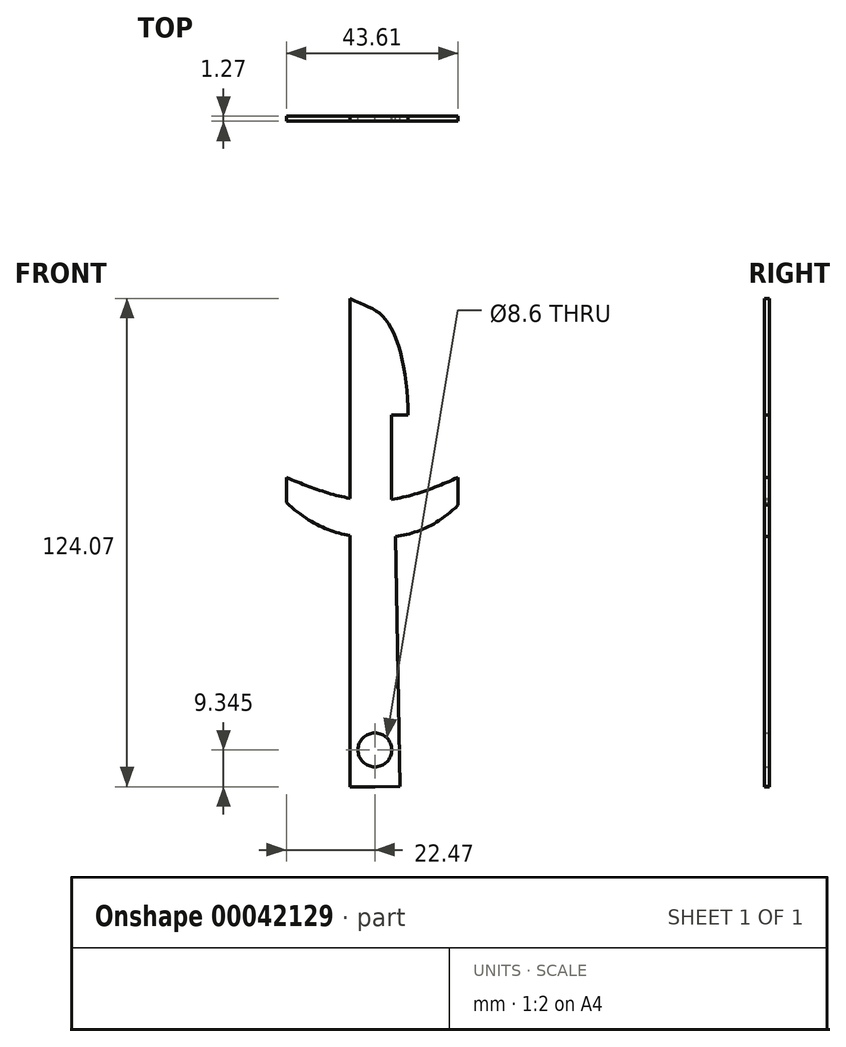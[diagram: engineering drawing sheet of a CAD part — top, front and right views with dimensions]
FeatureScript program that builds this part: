
annotation { "Feature Type Name" : "Feature", "Feature Type Description" : "" }
export const myFeature = defineFeature(function(context is Context, id is Id, definition is map)
    precondition{}
    {
        {
            var Q0;
            Q0=qCreatedBy(makeId("Front.planeOp"),FACE);
            var sketch = newSketch(context, id + "F0", { "sketchPlane" : qUnion([Q0])});
            skLineSegment(sketch, "E0", {"start": v(0, 0) * mm, "end": v(-6.35, 0) * mm});
            skLineSegment(sketch, "E1", {"start": v(0, 0) * mm, "end": v(6.35, 0.1) * mm});
            skFitSpline(sketch, "E2", {"points": [v(-22.47, 72.22) * mm, v(0, 63.3) * mm, v(21.14, 71.52) * mm], "startDerivative": vector(44.65, -42.56) * mm, "endDerivative": vector(42.56, 41.57) * mm});
            skLineSegment(sketch, "E3", {"start": v(-22.47, 72.22) * mm, "end": v(-22.47, 78.57) * mm});
            skLineSegment(sketch, "E4", {"start": v(21.14, 71.52) * mm, "end": v(21.14, 78.57) * mm});
            skFitSpline(sketch, "E5", {"points": [v(-22.47, 78.57) * mm, v(0, 72.7) * mm, v(21.14, 78.57) * mm], "startDerivative": vector(44.68, -19.03) * mm, "endDerivative": vector(42.53, 19.2) * mm});
            skPoint(sketch, "E6.end.orphan", {"position": v(17.01, 87.66) * mm});
            skPoint(sketch, "E7.start.orphan", {"position": v(12.12, 63.3) * mm});
            skPoint(sketch, "E8.start.orphan", {"position": v(-12.7, 63.3) * mm});
            skLineSegment(sketch, "E9", {"start": v(-6.35, 0) * mm, "end": v(-6.35, 63.83) * mm});
            skLineSegment(sketch, "E10", {"start": v(6.35, 0.1) * mm, "end": v(5.27, 63.6) * mm});
            skPoint(sketch, "E11.end.orphan", {"position": v(-6.75, 87.66) * mm});
            skLineSegment(sketch, "E12", {"start": v(-6.35, 124.07) * mm, "end": v(-6.35, 73.27) * mm});
            skPoint(sketch, "E13.orphan", {"position": v(0, 100.12) * mm});
            skPoint(sketch, "E14.orphan", {"position": v(5.27, 124.07) * mm});
            skPoint(sketch, "E15.1.internal.orphan", {"position": v(0, 137.97) * mm});
            skPoint(sketch, "E15.endDerivative.orphan", {"position": v(5.27, 97.92) * mm});
            skPoint(sketch, "E15.startDerivative.orphan", {"position": v(0, 124.07) * mm});
            skFitSpline(sketch, "E16", {"points": [v(-6.35, 124.07) * mm, v(2.83, 118.62) * mm, v(8.42, 94.4) * mm], "startDerivative": vector(31.7, -15.69) * mm, "endDerivative": vector(-0.61, -48.18) * mm});
            skLineSegment(sketch, "E17", {"start": v(8.42, 94.4) * mm, "end": v(4.2, 94.4) * mm});
            skLineSegment(sketch, "E18", {"start": v(4.2, 94.4) * mm, "end": v(4.2, 73) * mm});
            skPoint(sketch, "E19.orphan", {"position": v(0, 94.4) * mm});
            skCircle(sketch, "E20", {"center": v(0, 9.34) * mm, "radius": 4.3 * mm});
            skSolve(sketch);
        }
        {
            var Q0;
            Q0 = qSketchRegion(id + "F0", true);
            extrude(context, id + "F1", {"entities" : qUnion([Q0]), "depth" : 1.27 * mm});
        }
    });
